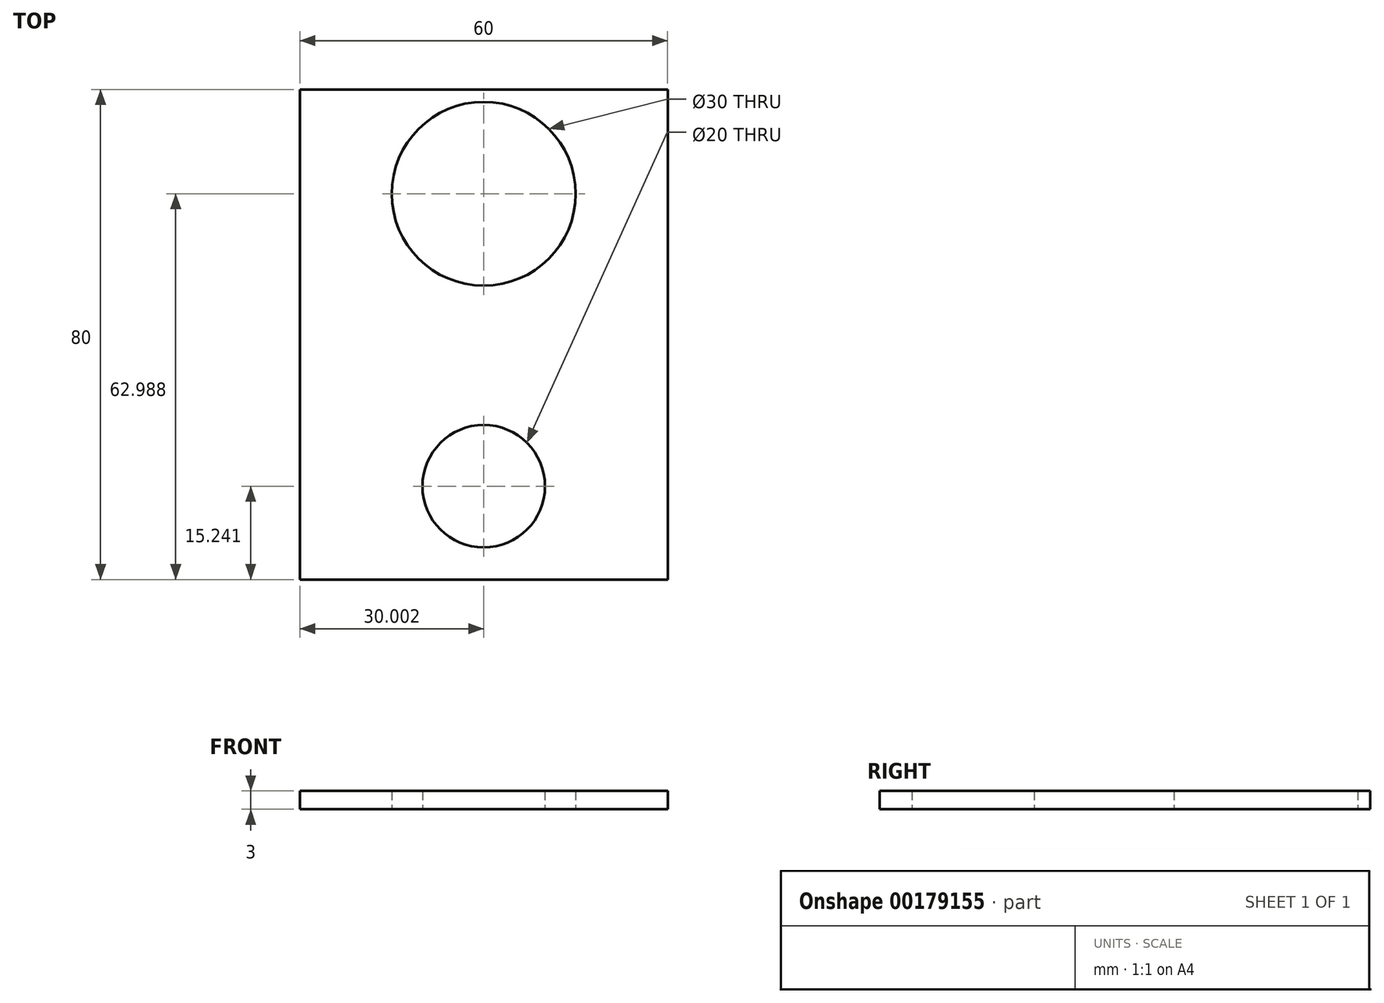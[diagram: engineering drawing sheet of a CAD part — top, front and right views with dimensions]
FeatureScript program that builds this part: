
annotation { "Feature Type Name" : "Feature", "Feature Type Description" : "" }
export const myFeature = defineFeature(function(context is Context, id is Id, definition is map)
    precondition{}
    {
        {
            var Q0;
            Q0=qCreatedBy(makeId("Top.planeOp"),FACE);
            var sketch = newSketch(context, id + "F0", { "sketchPlane" : qUnion([Q0])});
            skLineSegment(sketch, "E0.bottom", {"start": v(3.11, -28.9) * mm, "end": v(-56.89, -28.9) * mm});
            skLineSegment(sketch, "E0.top", {"start": v(3.11, 51.1) * mm, "end": v(-56.89, 51.1) * mm});
            skLineSegment(sketch, "E0.left", {"start": v(3.11, -28.9) * mm, "end": v(3.11, 51.1) * mm});
            skLineSegment(sketch, "E0.right", {"start": v(-56.89, -28.9) * mm, "end": v(-56.89, 51.1) * mm});
            skCircle(sketch, "E1", {"center": v(-26.89, 34.09) * mm, "radius": 15 * mm});
            skCircle(sketch, "E2", {"center": v(-26.89, -13.66) * mm, "radius": 10 * mm});
            skLineSegment(sketch, "E3", {"start": v(-26.89, 51.1) * mm, "end": v(-26.89, -28.9) * mm, "construction": true});
            skSolve(sketch);
        }
        {
            var Q0;
            Q0=makeQuery(id+"F0.imprint","IMPRINT",FACE,{"disambiguationData":[TD([[makeQuery(id+"F0.imprint","IMPRINT",EDGE,{"derivedFrom":sQuery(id+"F0.wireOp",EDGE,"E0.bottom")}),-1.0]])]});
            extrude(context, id + "F1", {"entities" : qUnion([Q0]), "depth" : 3 * mm});
        }
    });
